# Revit family: TY9226
name_source: partatom
category: Sprinklers
revit_build: Autodesk Revit 2016 (Build: 20150220_1215(x64)
units: mm (PartAtom-declared; Revit-internal decimal feet)

## family parameters
Always vertical = Yes
Cut with Voids When Loaded = No
Maintain Annotation Orientation = No
OmniClass Number = 23.65.70.17.11.24
OmniClass Title = Fire Fighting Sprinkler Heads
Part Type = Normal
Room Calculation Point = No
Round Connector Dimension = Use Diameter
Shared = No
Work Plane-Based = No

## types (4) — shared parameters
COBie = Yes
COBie.Component.Name = Sprinklers:ESFR Pendent_SIN
COBie.Type = Yes
COBie.Type.AssetType = Fixed
COBie.Type.Category = Pr_70_55_97_84:Sprinklers
COBie.Type.Colour = Yellow
COBie.Type.Finish = Brass
COBie.Type.Manufacturer = Tyco Fire Protection Products
COBie.Type.Material = Brass
COBie.Type.NominalHeight = 0' - 0"
COBie.Type.NominalLength = 0' - 0"
COBie.Type.NominalWidth = 0' - 0"
COBie.Type.Size = 1"(DN25)
COBie.Type.WarrantyGuarantorParts = http://tycofsbp.com
Coverage = Standard
K-Factor = 24.9717
Manufacturer = Tyco Fire Protection Products
Manufacturer URL = www.tyco-fire.com
Model = ESFR-25
Nominal Diameter 1 = 1"
Orifice = Extra Large
Orifice Size = 1"
Outside Diameter 1 = 1"
Response = Quick
SIN No = TY9226
Takeout 1 = 4"
Technical Data Sheet No = TFP312
zero-valued in all types: COBie.Type.ReplacementCost, Style Id

## per-type parameters (varying)
| type | COBie.Component.Description | COBie.Type.DurationUnit | COBie.Type.ModelNumber | COBie.Type.ModelReference | COBie.Type.Shape | Part No | Temperature Rating |
| ESFR-25 Wet ESFR Pendent_Brass_165  73.9°C K360 DN25 NPT Br_58-441-1-165 | ESFR-25 Wet ESFR Pendent  165°F K25.2 1 NPT Br | Year | 58-441-1-165 | ESFR-25 Wet ESFR Pendent  165°F K25.2 1 NPT Br | Cylinder | 58-441-1-165 | 165 °F |
| ESFR-25 Wet ESFR Pendent_Brass_214  100°C K360 DN25 NPT Br_58-441-1-214 | ESFR-25 Wet ESFR Pendent  212°F K25.2 1 NPT Br | year | 58-441-1-214 | ESFR-25 Wet ESFR Pendent  212°F K25.2 1 NPT Br | Cylinder | 58-441-1-214 | 212 °F |
| ESFR-25 Wet ESFR Pendent_Brass_165  100°C K360 DN25 ISO Br_58-442-1-165 | ESFR-25 Wet ESFR Pendent_Brass_214  212°F K25.2 1 ISO Br | year | 58-442-1-214 | ESFR-25 Wet ESFR Pendent_Brass_214  212°F K25.2 1 ISO Br | Cylider | 58-442-1-165 | 212 °F |
| ESFR-25 Wet ESFR Pendent_Brass_214  100°C K360 DN25 ISO Br_58-442-1-214 | ESFR-25 Wet ESFR Pendent_Brass_214  212°F K25.2 1 ISO Br | year | 58-442-1-214 | ESFR-25 Wet ESFR Pendent_Brass_214  212°F K25.2 1 ISO Br | Cylinder | 58-442-1-214 | 212 °F |

note: column(s) folded — value = type name in every type: Description

## geometry (parser evidence)
native form markers: Blend x2, Sweep x47
no freeform markers — native parametric forms only
